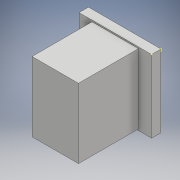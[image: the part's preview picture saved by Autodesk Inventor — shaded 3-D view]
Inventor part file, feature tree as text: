
AUTODESK INVENTOR PART (.ipt)
format: ipt  version: 2017 (Build 210142000, 142)  size: 102,400 bytes
history: native  units: mm
features: sketch x6, extrude x2, other x1
ambient origin geometry x8: Origin, YZ Plane, XZ Plane, XY Plane, X Axis, Y Axis, Z Axis, Center Point
bodies: Body1 (feature_tree)
feature tree (9):
  other  "ソリッド1"
  extrude  "押し出し1"  Depth=0.5mm
  sketch  "スケッチ2"
  extrude  "押し出し2"  Depth=0.5mm
  sketch  "スケッチ4"
  sketch  "スケッチ5"
  sketch  "スケッチ6"
  sketch  "スケッチ1"
  sketch  "スケッチ3"
